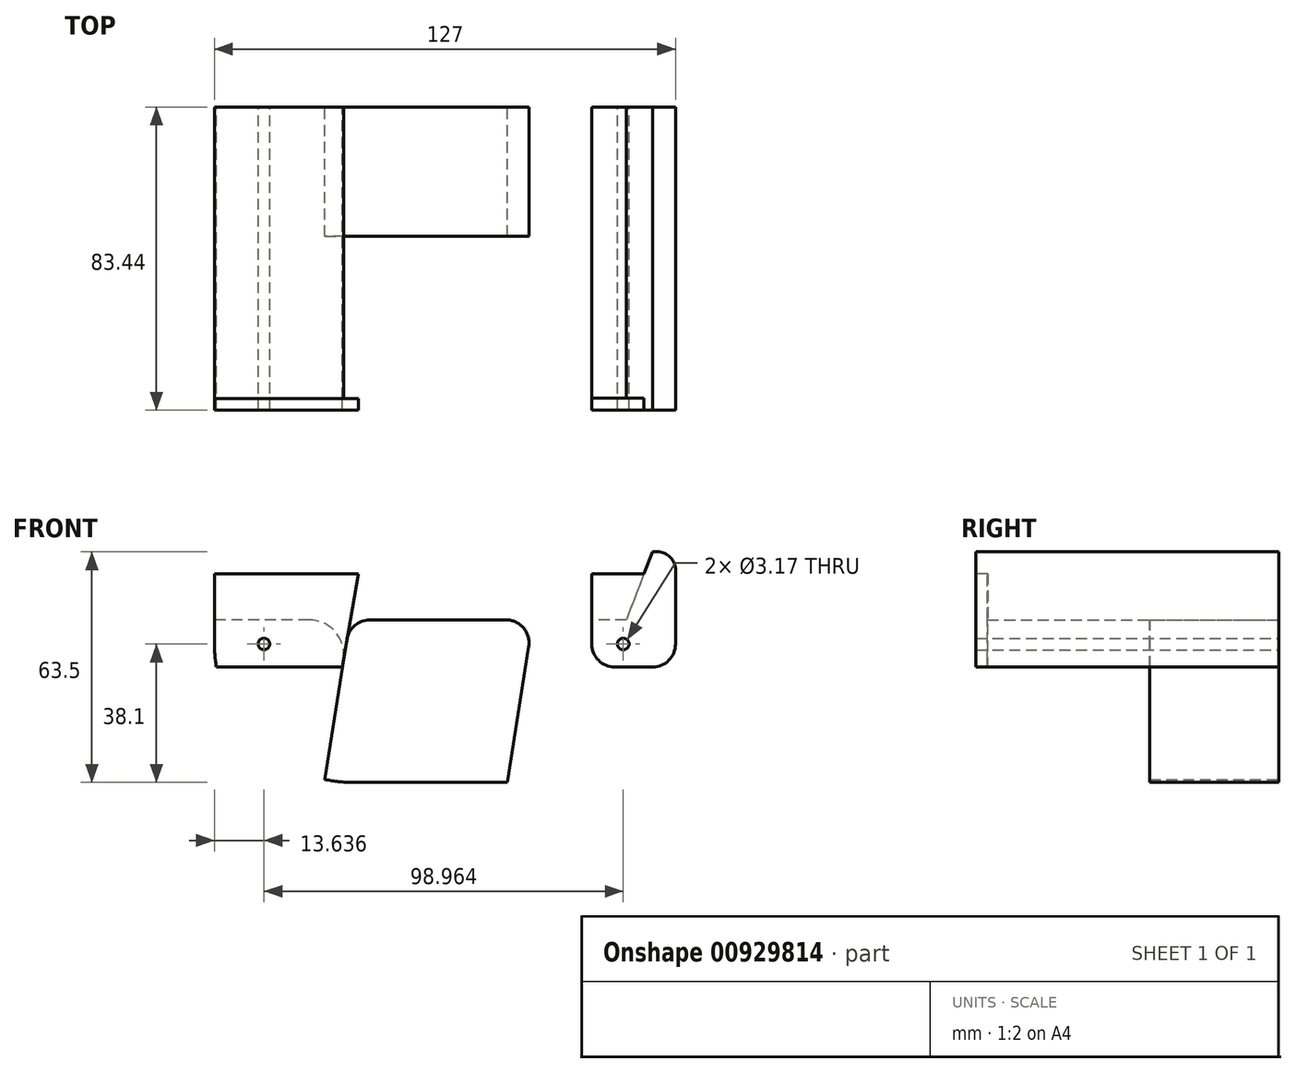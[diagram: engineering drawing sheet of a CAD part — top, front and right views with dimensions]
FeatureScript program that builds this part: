
annotation { "Feature Type Name" : "Feature", "Feature Type Description" : "" }
export const myFeature = defineFeature(function(context is Context, id is Id, definition is map)
    precondition{}
    {
        {
            var Q0;
            Q0=qCreatedBy(makeId("Right.planeOp"),FACE);
            var sketch = newSketch(context, id + "F0", { "sketchPlane" : qUnion([Q0])});
            skLineSegment(sketch, "E0.bottom", {"start": v(-39.69, -26.99) * mm, "end": v(39.69, -26.99) * mm});
            skLineSegment(sketch, "E0.top", {"start": v(-39.69, 26.99) * mm, "end": v(39.69, 26.99) * mm});
            skLineSegment(sketch, "E0.left", {"start": v(-39.69, -26.99) * mm, "end": v(-39.69, 26.99) * mm});
            skLineSegment(sketch, "E0.right", {"start": v(39.69, -26.99) * mm, "end": v(39.69, 26.99) * mm});
            skPoint(sketch, "E0.middle", {"position": v(0, 0) * mm});
            skLineSegment(sketch, "E1.bottom", {"start": v(-19.05, 26.99) * mm, "end": v(19.05, 26.99) * mm});
            skLineSegment(sketch, "E1.top", {"start": v(-19.05, 128.59) * mm, "end": v(19.05, 128.59) * mm});
            skLineSegment(sketch, "E1.left", {"start": v(-19.05, 26.99) * mm, "end": v(-19.05, 128.59) * mm});
            skLineSegment(sketch, "E1.right", {"start": v(19.05, 26.99) * mm, "end": v(19.05, 128.59) * mm});
            skLineSegment(sketch, "E2.bottom", {"start": v(-28.58, 217.49) * mm, "end": v(28.57, 217.49) * mm});
            skLineSegment(sketch, "E2.top", {"start": v(-28.58, 128.59) * mm, "end": v(28.57, 128.59) * mm});
            skLineSegment(sketch, "E2.left", {"start": v(-28.58, 217.49) * mm, "end": v(-28.58, 128.59) * mm});
            skLineSegment(sketch, "E2.right", {"start": v(28.57, 217.49) * mm, "end": v(28.57, 128.59) * mm});
            skSolve(sketch);
        }
        {
            var Q0;
            Q0=qCreatedBy(makeId("Front.planeOp"),FACE);
            var sketch = newSketch(context, id + "F1", { "sketchPlane" : qUnion([Q0])});
            skLineSegment(sketch, "E3.bottom", {"start": v(-25.4, -31.75) * mm, "end": v(25.4, -31.75) * mm});
            skLineSegment(sketch, "E3.top", {"start": v(-50.8, 31.75) * mm, "end": v(58.42, 31.75) * mm});
            skLineSegment(sketch, "E3.left", {"start": v(-63.5, 6.35) * mm, "end": v(-63.5, 19.05) * mm});
            skLineSegment(sketch, "E3.right", {"start": v(63.5, 6.35) * mm, "end": v(63.5, 26.67) * mm});
            skPoint(sketch, "E3.middle", {"position": v(0, 0) * mm});
            skLineSegment(sketch, "E4", {"start": v(57.15, 31.75) * mm, "end": v(49.95, 13) * mm});
            skLineSegment(sketch, "E5", {"start": v(49.95, 13) * mm, "end": v(40.43, 13) * mm});
            skLineSegment(sketch, "E6", {"start": v(40.43, 13) * mm, "end": v(40.43, 0) * mm});
            skLineSegment(sketch, "E7", {"start": v(40.43, 0) * mm, "end": v(63.5, 0) * mm});
            skLineSegment(sketch, "E8", {"start": v(-63.5, 0) * mm, "end": v(-28.3, 0) * mm});
            skLineSegment(sketch, "E9", {"start": v(-28.3, 0) * mm, "end": v(-28, 1.99) * mm});
            skLineSegment(sketch, "E10", {"start": v(-37.4, 13) * mm, "end": v(-63.5, 13) * mm});
            skLineSegment(sketch, "E11", {"start": v(-63.5, 13) * mm, "end": v(-41.2, 13) * mm});
            skPoint(sketch, "E12.visualSharp", {"position": v(-26.25, 13) * mm});
            skArc(sketch, "E12.filletArc", {"start": v(-28, 1.99) * mm, "mid": v(-30.16, 9.66) * mm, "end": v(-37.4, 13) * mm});
            skLineSegment(sketch, "E13", {"start": v(-26.13, 13) * mm, "end": v(-33.19, -31.75) * mm});
            skLineSegment(sketch, "E14", {"start": v(-33.19, -31.75) * mm, "end": v(17.16, -31.75) * mm});
            skLineSegment(sketch, "E15", {"start": v(17.16, -31.75) * mm, "end": v(24.21, 13) * mm});
            skLineSegment(sketch, "E16", {"start": v(24.21, 13) * mm, "end": v(-26.13, 13) * mm});
            skPoint(sketch, "E17.visualSharp", {"position": v(-63.5, 31.75) * mm});
            skArc(sketch, "E17.filletArc", {"start": v(-50.8, 31.75) * mm, "mid": v(-59.78, 28.03) * mm, "end": v(-63.5, 19.05) * mm});
            skPoint(sketch, "E18.visualSharp", {"position": v(-63.5, -31.75) * mm});
            skArc(sketch, "E18.filletArc", {"start": v(-63.5, 6.35) * mm, "mid": v(-52.34, -20.6) * mm, "end": v(-25.4, -31.75) * mm});
            skPoint(sketch, "E19.visualSharp", {"position": v(63.5, -31.75) * mm});
            skArc(sketch, "E19.filletArc", {"start": v(25.4, -31.75) * mm, "mid": v(52.34, -20.6) * mm, "end": v(63.5, 6.35) * mm});
            skPoint(sketch, "E20.visualSharp", {"position": v(63.5, 31.75) * mm});
            skArc(sketch, "E20.filletArc", {"start": v(63.5, 26.67) * mm, "mid": v(62.01, 30.26) * mm, "end": v(58.42, 31.75) * mm});
            skCircle(sketch, "E21", {"center": v(-49.86, 6.35) * mm, "radius": 1.59 * mm});
            skCircle(sketch, "E22", {"center": v(49.1, 6.35) * mm, "radius": 1.59 * mm});
            skSolve(sketch);
        }
        {
            var Q0;
            {var subQ8=sQuery(id+"F1.wireOp",EDGE,"E3.bottom");Q0=makeQuery(id+"F1.imprint","IMPRINT",FACE,{"disambiguationData":[TD([[makeQuery(id+"F1.imprint","IMPRINT",EDGE,{"derivedFrom":subQ8}),1.0]])]});}
            extrude(context, id + "F2", {"entities" : qUnion([Q0]), "depth" : 12.7 * mm, "offsetDistance" : 25.4 * mm});
        }
        {
            var Q0;
            {var subQ0=sQuery(id+"F1.wireOp",EDGE,"E9");Q0=makeQuery(id+"F1.imprint","IMPRINT",FACE,{"disambiguationData":[TD([[makeQuery(id+"F1.imprint","IMPRINT",EDGE,{"derivedFrom":subQ0}),1.0]])]});}
            var Q1;
            {var subQ1=sQuery(id+"F1.wireOp",EDGE,"E3.right");Q1=makeQuery(id+"F1.imprint","IMPRINT",FACE,{"disambiguationData":[TD([[makeQuery(id+"F1.imprint","IMPRINT",EDGE,{"derivedFrom":subQ1}),1.0]])]});}
            extrude(context, id + "F3", {"entities" : qUnion([Q0, Q1]), "operationType" : NewBodyOperationType.ADD, "depth" : 54.86 * mm, "offsetDistance" : 25.4 * mm});
        }
        {
            var Q0;
            {var subQ0=sQuery(id+"F1.wireOp",EDGE,"E15");Q0=makeQuery(id+"F1.imprint","IMPRINT",FACE,{"disambiguationData":[TD([[makeQuery(id+"F1.imprint","IMPRINT",EDGE,{"derivedFrom":subQ0}),1.0]])]});}
            extrude(context, id + "F4", {"entities" : qUnion([Q0]), "operationType" : NewBodyOperationType.ADD, "depth" : 35.56 * mm, "offsetDistance" : 25.4 * mm});
        }
        {
            var Q0;
            Q0=makeQuery(id+"F3.opExtrude","CAP_FACE",FACE,{"disambiguationData":[OSD([sQuery(id+"F1.wireOp",EDGE,"E3.top"),sQuery(id+"F1.wireOp",EDGE,"E3.right"),sQuery(id+"F1.wireOp",EDGE,"E4"),sQuery(id+"F1.wireOp",EDGE,"E5"),sQuery(id+"F1.wireOp",EDGE,"E6"),sQuery(id+"F1.wireOp",EDGE,"E7"),sQuery(id+"F1.wireOp",EDGE,"E19.filletArc"),sQuery(id+"F1.wireOp",EDGE,"E20.filletArc"),sQuery(id+"F1.wireOp",EDGE,"E22")])],"isStart":false});
            var Q1;
            Q1=makeQuery(id+"F3.opExtrude","CAP_FACE",FACE,{"disambiguationData":[OSD([sQuery(id+"F1.wireOp",EDGE,"E3.left"),sQuery(id+"F1.wireOp",EDGE,"E8"),sQuery(id+"F1.wireOp",EDGE,"E9"),sQuery(id+"F1.wireOp",EDGE,"E10"),sQuery(id+"F1.wireOp",EDGE,"E11"),sQuery(id+"F1.wireOp",EDGE,"E12.filletArc"),sQuery(id+"F1.wireOp",EDGE,"E18.filletArc"),sQuery(id+"F1.wireOp",EDGE,"E21")])],"isStart":false});
            extrude(context, id + "F5", {"entities" : qUnion([Q0, Q1]), "operationType" : NewBodyOperationType.ADD, "depth" : 28.57 * mm, "offsetDistance" : 25.4 * mm});
        }
        {
            var Q0;
            Q0=makeQuery(id+"F5.opExtrude","CAP_FACE",FACE,{"disambiguationData":[OSD([sQuery(id+"F1.wireOp",EDGE,"E3.top"),sQuery(id+"F1.wireOp",EDGE,"E3.right"),sQuery(id+"F1.wireOp",EDGE,"E4"),sQuery(id+"F1.wireOp",EDGE,"E5"),sQuery(id+"F1.wireOp",EDGE,"E6"),sQuery(id+"F1.wireOp",EDGE,"E7"),sQuery(id+"F1.wireOp",EDGE,"E19.filletArc"),sQuery(id+"F1.wireOp",EDGE,"E20.filletArc"),sQuery(id+"F1.wireOp",EDGE,"E22")])],"isStart":false});
            var sketch = newSketch(context, id + "F6", { "sketchPlane" : qUnion([Q0])});
            skLineSegment(sketch, "E23", {"start": v(40.43, 13) * mm, "end": v(40.43, 25.7) * mm});
            skLineSegment(sketch, "E24", {"start": v(40.43, 25.7) * mm, "end": v(54.83, 25.7) * mm});
            skSolve(sketch);
        }
        {
            var Q0;
            Q0=makeQuery(id+"F6.imprint","IMPRINT",FACE,{"disambiguationData":[TD([[makeQuery(id+"F6.imprint","IMPRINT",EDGE,{"derivedFrom":sQuery(id+"F6.wireOp",EDGE,"E23")}),-1.0]])]});
            extrude(context, id + "F7", {"entities" : qUnion([Q0]), "operationType" : NewBodyOperationType.ADD, "depth" : -3.25 * mm, "offsetDistance" : 25.4 * mm});
        }
        {
            var Q0;
            Q0=makeQuery(id+"F5.opExtrude","CAP_FACE",FACE,{"disambiguationData":[OSD([sQuery(id+"F1.wireOp",EDGE,"E3.left"),sQuery(id+"F1.wireOp",EDGE,"E8"),sQuery(id+"F1.wireOp",EDGE,"E9"),sQuery(id+"F1.wireOp",EDGE,"E10"),sQuery(id+"F1.wireOp",EDGE,"E11"),sQuery(id+"F1.wireOp",EDGE,"E12.filletArc"),sQuery(id+"F1.wireOp",EDGE,"E18.filletArc"),sQuery(id+"F1.wireOp",EDGE,"E21")])],"isStart":false});
            var sketch = newSketch(context, id + "F8", { "sketchPlane" : qUnion([Q0])});
            skLineSegment(sketch, "E25", {"start": v(-63.5, 13) * mm, "end": v(-63.5, 25.7) * mm});
            skLineSegment(sketch, "E26", {"start": v(-63.5, 25.7) * mm, "end": v(-23.9, 25.7) * mm});
            skLineSegment(sketch, "E27", {"start": v(-23.9, 25.7) * mm, "end": v(-28.3, 0) * mm});
            skSolve(sketch);
        }
        {
            var Q0;
            Q0=makeQuery(id+"F8.imprint","IMPRINT",FACE,{"disambiguationData":[TD([[makeQuery(id+"F8.imprint","IMPRINT",EDGE,{"derivedFrom":sQuery(id+"F8.wireOp",EDGE,"E25")}),-1.0]])]});
            extrude(context, id + "F9", {"entities" : qUnion([Q0]), "operationType" : NewBodyOperationType.ADD, "depth" : -3.17 * mm, "offsetDistance" : 25.4 * mm});
        }
        {
            var Q0;
            Q0=makeQuery(id+"F9.opExtrude","SWEPT_EDGE",EDGE,{"disambiguationData":[OSD([sQuery(id+"F8.wireOp",EDGE,"E25"),sQuery(id+"F8.wireOp",EDGE,"E26")])]});
            var Q1;
            Q1=makeQuery(id+"F9.opExtrude","SWEPT_EDGE",EDGE,{"disambiguationData":[OSD([sQuery(id+"F8.wireOp",EDGE,"E26"),sQuery(id+"F8.wireOp",EDGE,"E27")])]});
            var Q2;
            {var subQ0=sQuery(id+"F1.wireOp",EDGE,"E18.filletArc");var subQ1=sQuery(id+"F1.wireOp",EDGE,"E8");Q2=makeQuery(id+"F5.boolean.opBoolean","MERGE",EDGE,{"derivedFrom":[makeQuery(id+"F3.opExtrude","SWEPT_EDGE",EDGE,{"disambiguationData":[OSD([subQ1,subQ0])]}),makeQuery(id+"F5.opExtrude","SWEPT_EDGE",EDGE,{"disambiguationData":[OSD([subQ1,subQ0])]})]});}
            var Q3;
            {var subQ0=sQuery(id+"F1.wireOp",EDGE,"E9");var subQ1=sQuery(id+"F1.wireOp",EDGE,"E8");Q3=makeQuery(id+"F9.boolean.opBoolean","MERGE",EDGE,{"derivedFrom":[makeQuery(id+"F5.boolean.opBoolean","MERGE",EDGE,{"derivedFrom":[makeQuery(id+"F3.opExtrude","SWEPT_EDGE",EDGE,{"disambiguationData":[OSD([subQ1,subQ0])]}),makeQuery(id+"F5.opExtrude","SWEPT_EDGE",EDGE,{"disambiguationData":[OSD([subQ1,subQ0])]})]}),makeQuery(id+"F9.opExtrude","SWEPT_EDGE",EDGE,{"disambiguationData":[OSD([subQ1,subQ0,sQuery(id+"F8.wireOp",EDGE,"E27")])]})]});}
            var Q4;
            {var subQ0=sQuery(id+"F1.wireOp",EDGE,"E7");var subQ1=sQuery(id+"F1.wireOp",EDGE,"E6");Q4=makeQuery(id+"F5.boolean.opBoolean","MERGE",EDGE,{"derivedFrom":[makeQuery(id+"F3.opExtrude","SWEPT_EDGE",EDGE,{"disambiguationData":[OSD([subQ1,subQ0])]}),makeQuery(id+"F5.opExtrude","SWEPT_EDGE",EDGE,{"disambiguationData":[OSD([subQ1,subQ0])]})]});}
            var Q5;
            {var subQ0=sQuery(id+"F1.wireOp",EDGE,"E19.filletArc");var subQ1=sQuery(id+"F1.wireOp",EDGE,"E7");Q5=makeQuery(id+"F5.boolean.opBoolean","MERGE",EDGE,{"derivedFrom":[makeQuery(id+"F3.opExtrude","SWEPT_EDGE",EDGE,{"disambiguationData":[OSD([subQ1,subQ0])]}),makeQuery(id+"F5.opExtrude","SWEPT_EDGE",EDGE,{"disambiguationData":[OSD([subQ1,subQ0])]})]});}
            var Q6;
            Q6=makeQuery(id+"F4.opExtrude","SWEPT_EDGE",EDGE,{"disambiguationData":[OSD([sQuery(id+"F1.wireOp",EDGE,"E15"),sQuery(id+"F1.wireOp",EDGE,"E16")])]});
            var Q7;
            Q7=makeQuery(id+"F4.opExtrude","SWEPT_EDGE",EDGE,{"disambiguationData":[OSD([sQuery(id+"F1.wireOp",EDGE,"E13"),sQuery(id+"F1.wireOp",EDGE,"E16")])]});
            fillet(context, id + "F10", {"entities" : qUnion([Q0, Q1, Q2, Q3, Q4, Q5, Q6, Q7]), "radius" : 6.35 * mm, "tangentPropagation" : true, "allowEdgeOverflow" : false});
        }
    });
